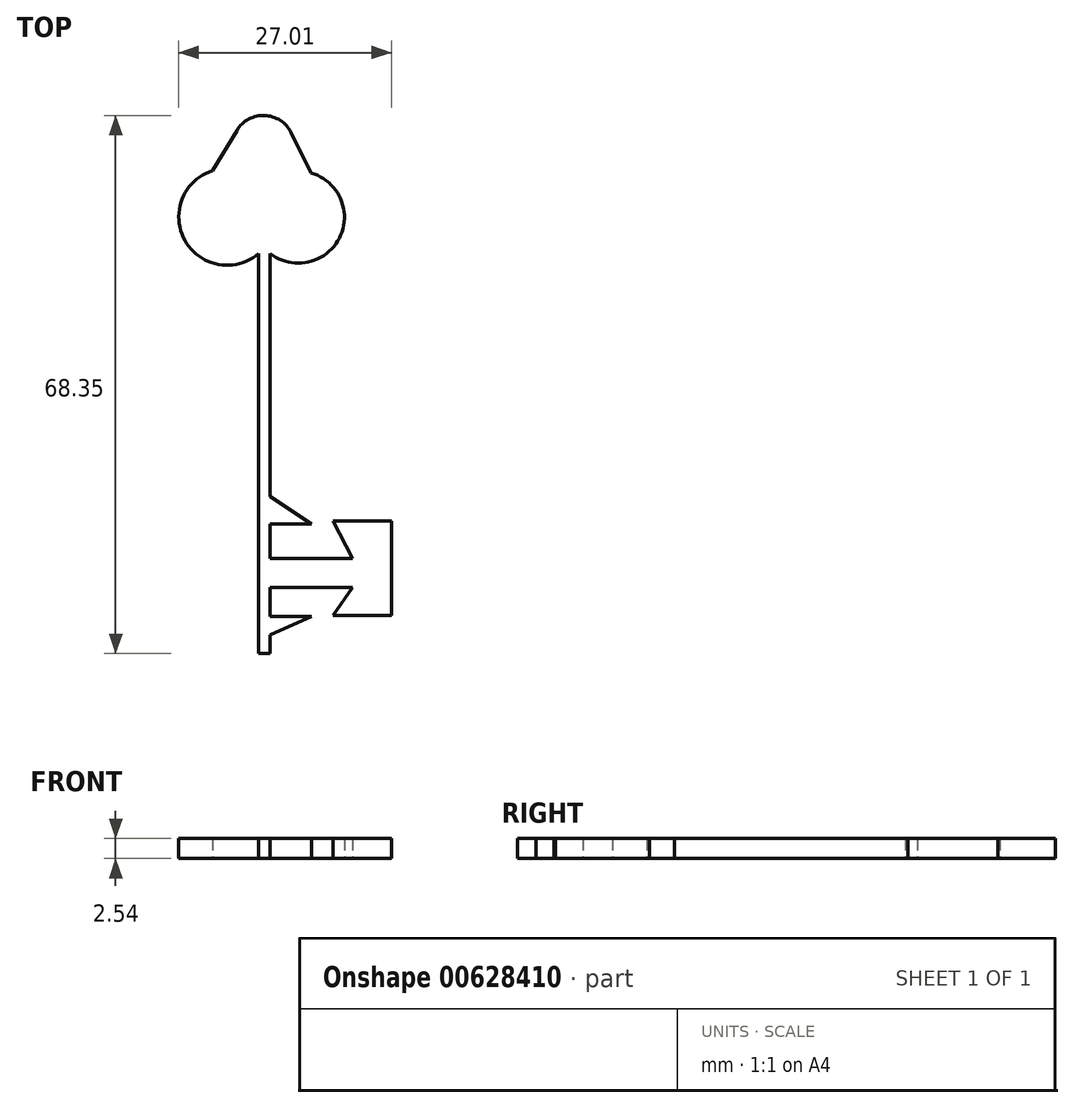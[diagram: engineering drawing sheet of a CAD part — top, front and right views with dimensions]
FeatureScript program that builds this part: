
annotation { "Feature Type Name" : "Feature", "Feature Type Description" : "" }
export const myFeature = defineFeature(function(context is Context, id is Id, definition is map)
    precondition{}
    {
        {
            var Q0;
            Q0=qCreatedBy(makeId("Top.planeOp"),FACE);
            var sketch = newSketch(context, id + "F0", { "sketchPlane" : qUnion([Q0])});
            skCircle(sketch, "E0", {"center": v(-30.17, 43.06) * mm, "radius": 4.4 * mm});
            skArc(sketch, "E1", {"start": v(-30.3, 47.46) * mm, "mid": v(-41.03, 43.83) * mm, "end": v(-30.9, 38.73) * mm});
            skArc(sketch, "E2", {"start": v(-29.43, 38.73) * mm, "mid": v(-20.02, 43.78) * mm, "end": v(-30.04, 47.46) * mm});
            skCircle(sketch, "E3", {"center": v(-30.3, 52.35) * mm, "radius": 3.93 * mm});
            skLineSegment(sketch, "E4", {"start": v(-36.76, 49.25) * mm, "end": v(-33.66, 54.39) * mm});
            skLineSegment(sketch, "E5", {"start": v(-24.21, 48.98) * mm, "end": v(-26.78, 54.11) * mm});
            skLineSegment(sketch, "E6", {"start": v(-30.9, 38.73) * mm, "end": v(-30.9, -7.4) * mm});
            skLineSegment(sketch, "E7", {"start": v(-29.43, 38.73) * mm, "end": v(-29.43, -7.4) * mm});
            skLineSegment(sketch, "E8", {"start": v(-29.43, 0) * mm, "end": v(-18.95, 0) * mm});
            skLineSegment(sketch, "E9", {"start": v(-18.95, 0) * mm, "end": v(-21.45, 4.73) * mm});
            skLineSegment(sketch, "E10", {"start": v(-21.45, 4.73) * mm, "end": v(-14.03, 4.73) * mm});
            skLineSegment(sketch, "E11", {"start": v(-14.03, 4.73) * mm, "end": v(-14.03, -4.4) * mm});
            skLineSegment(sketch, "E12", {"start": v(-14.03, -4.4) * mm, "end": v(-14.03, -7.22) * mm});
            skLineSegment(sketch, "E13", {"start": v(-14.03, -7.22) * mm, "end": v(-21.45, -7.22) * mm});
            skLineSegment(sketch, "E14", {"start": v(-21.45, -7.22) * mm, "end": v(-18.95, -3.7) * mm});
            skLineSegment(sketch, "E15", {"start": v(-18.95, -3.7) * mm, "end": v(-29.43, -3.7) * mm});
            skLineSegment(sketch, "E16", {"start": v(-29.43, 7.9) * mm, "end": v(-24.2, 4.38) * mm});
            skPoint(sketch, "E16.endSnap0", {"position": v(-24.2, 0) * mm});
            skLineSegment(sketch, "E17", {"start": v(-24.2, 4.38) * mm, "end": v(-29.43, 4.38) * mm});
            skLineSegment(sketch, "E18", {"start": v(-30.9, 38.73) * mm, "end": v(-29.43, 38.73) * mm});
            skLineSegment(sketch, "E19", {"start": v(-29.43, -7.4) * mm, "end": v(-29.43, -12.07) * mm});
            skLineSegment(sketch, "E20", {"start": v(-30.9, -7.4) * mm, "end": v(-30.9, -12.07) * mm});
            skLineSegment(sketch, "E21", {"start": v(-30.9, -12.07) * mm, "end": v(-29.43, -12.07) * mm});
            skLineSegment(sketch, "E22", {"start": v(-29.43, -7.4) * mm, "end": v(-24.2, -7.4) * mm});
            skPoint(sketch, "E22.endSnap0", {"position": v(-24.2, -3.7) * mm});
            skLineSegment(sketch, "E23", {"start": v(-29.43, -9.73) * mm, "end": v(-29.43, -7.4) * mm});
            skLineSegment(sketch, "E24", {"start": v(-29.43, 4.38) * mm, "end": v(-29.43, 7.9) * mm});
            skLineSegment(sketch, "E25", {"start": v(-24.2, -7.4) * mm, "end": v(-29.43, -9.73) * mm});
            skSolve(sketch);
        }
        {
            var Q0;
            {var subQ0=sQuery(id+"F0.wireOp",EDGE,"E8");Q0=makeQuery(id+"F0.imprint","IMPRINT",FACE,{"disambiguationData":[TD([[makeQuery(id+"F0.imprint","IMPRINT",EDGE,{"derivedFrom":subQ0}),-1.0]])]});}
            var Q1;
            Q1=makeQuery(id+"F0.imprint","IMPRINT",FACE,{"disambiguationData":[TD([[makeQuery(id+"F0.imprint","IMPRINT",EDGE,{"derivedFrom":sQuery(id+"F0.wireOp",EDGE,"E16")}),-1.0]])]});
            var Q2;
            Q2=makeQuery(id+"F0.imprint","IMPRINT",FACE,{"disambiguationData":[TD([[makeQuery(id+"F0.imprint","IMPRINT",EDGE,{"derivedFrom":sQuery(id+"F0.wireOp",EDGE,"E22")}),-1.0]])]});
            var Q3;
            {var subQ0=sQuery(id+"F0.wireOp",EDGE,"E18");Q3=makeQuery(id+"F0.imprint","IMPRINT",FACE,{"disambiguationData":[TD([[makeQuery(id+"F0.imprint","IMPRINT",EDGE,{"derivedFrom":subQ0}),-1.0]])]});}
            var Q4;
            {var subQ5=sQuery(id+"F0.wireOp",EDGE,"E18");Q4=makeQuery(id+"F0.imprint","IMPRINT",FACE,{"disambiguationData":[TD([[makeQuery(id+"F0.imprint","IMPRINT",EDGE,{"derivedFrom":subQ5}),1.0]])]});}
            var Q5;
            {var subQ4=sQuery(id+"F0.wireOp",EDGE,"E4");Q5=makeQuery(id+"F0.imprint","IMPRINT",FACE,{"disambiguationData":[TD([[makeQuery(id+"F0.imprint","IMPRINT",EDGE,{"derivedFrom":subQ4}),-1.0]])]});}
            var Q6;
            {var subQ4=sQuery(id+"F0.wireOp",EDGE,"E6");Q6=makeQuery(id+"F0.imprint","IMPRINT",FACE,{"disambiguationData":[TD([[makeQuery(id+"F0.imprint","IMPRINT",EDGE,{"derivedFrom":subQ4}),1.0]])]});}
            var Q7;
            {var subQ0=sQuery(id+"F0.wireOp",EDGE,"E1");var subQ1=sQuery(id+"F0.wireOp",EDGE,"E0");var subQ2=makeQuery(id+"F0.imprint","INTERSECT",VERTEX,{"derivedFrom":[subQ1,subQ0]});Q7=makeQuery(id+"F0.imprint","IMPRINT",FACE,{"disambiguationData":[TD([[makeQuery(id+"F0.imprint","IMPRINT",EDGE,{"disambiguationData":[TD([[subQ2,-1.0]])],"derivedFrom":subQ0}),1.0]])]});}
            var Q8;
            {var subQ0=sQuery(id+"F0.wireOp",EDGE,"E2");var subQ1=sQuery(id+"F0.wireOp",EDGE,"E0");var subQ3=makeQuery(id+"F0.imprint","INTERSECT",VERTEX,{"derivedFrom":[subQ1,subQ0]});Q8=makeQuery(id+"F0.imprint","IMPRINT",FACE,{"disambiguationData":[TD([[makeQuery(id+"F0.imprint","IMPRINT",EDGE,{"disambiguationData":[TD([[subQ3,1.0]])],"derivedFrom":subQ0}),1.0]])]});}
            var Q9;
            {var subQ0=sQuery(id+"F0.wireOp",EDGE,"E3");var subQ1=makeQuery(id+"F0.imprint","INTERSECT",VERTEX,{"derivedFrom":[subQ0,sQuery(id+"F0.wireOp",EDGE,"E4")]});Q9=makeQuery(id+"F0.imprint","IMPRINT",FACE,{"disambiguationData":[TD([[makeQuery(id+"F0.imprint","IMPRINT",EDGE,{"disambiguationData":[TD([[subQ1,1.0]])],"derivedFrom":subQ0}),1.0]])]});}
            extrude(context, id + "F1", {"entities" : qUnion([Q0, Q1, Q2, Q3, Q4, Q5, Q6, Q7, Q8, Q9]), "depth" : 2.54 * mm, "offsetDistance" : 25.4 * mm});
        }
    });
